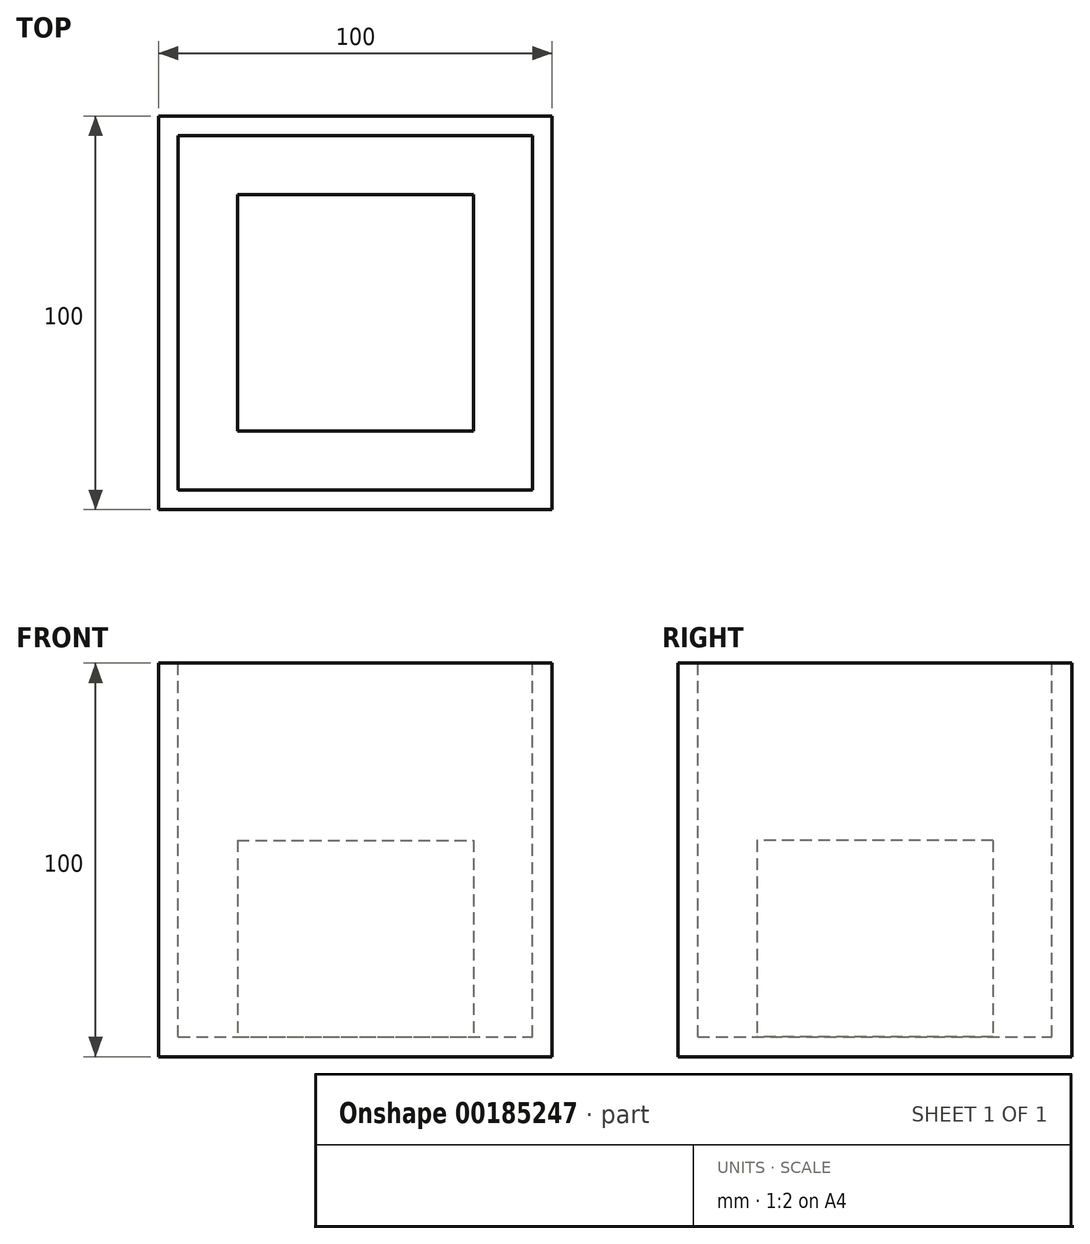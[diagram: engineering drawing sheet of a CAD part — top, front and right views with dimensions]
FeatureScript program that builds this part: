
annotation { "Feature Type Name" : "Feature", "Feature Type Description" : "" }
export const myFeature = defineFeature(function(context is Context, id is Id, definition is map)
    precondition{}
    {
        {
            var Q0;
            Q0=qCreatedBy(makeId("Top.planeOp"),FACE);
            var sketch = newSketch(context, id + "F0", { "sketchPlane" : qUnion([Q0])});
            skLineSegment(sketch, "E0.bottom", {"start": v(0, 0) * mm, "end": v(100, 0) * mm});
            skLineSegment(sketch, "E0.top", {"start": v(0, 100) * mm, "end": v(100, 100) * mm});
            skLineSegment(sketch, "E0.left", {"start": v(0, 0) * mm, "end": v(0, 100) * mm});
            skLineSegment(sketch, "E0.right", {"start": v(100, 0) * mm, "end": v(100, 100) * mm});
            skSolve(sketch);
        }
        {
            var Q0;
            Q0 = qSketchRegion(id + "F0", true);
            extrude(context, id + "F1", {"entities" : qUnion([Q0]), "depth" : 100 * mm});
        }
        {
            var Q0;
            Q0=makeQuery(id+"F1.opExtrude","CAP_FACE",FACE,{"disambiguationData":[OSD([sQuery(id+"F0.wireOp",EDGE,"E0.bottom"),sQuery(id+"F0.wireOp",EDGE,"E0.top"),sQuery(id+"F0.wireOp",EDGE,"E0.left"),sQuery(id+"F0.wireOp",EDGE,"E0.right")])],"isStart":false});
            var sketch = newSketch(context, id + "F2", { "sketchPlane" : qUnion([Q0])});
            skLineSegment(sketch, "E1.bottom", {"start": v(5, 5) * mm, "end": v(95, 5) * mm});
            skLineSegment(sketch, "E1.top", {"start": v(5, 95) * mm, "end": v(95, 95) * mm});
            skLineSegment(sketch, "E1.left", {"start": v(5, 5) * mm, "end": v(5, 95) * mm});
            skLineSegment(sketch, "E1.right", {"start": v(95, 5) * mm, "end": v(95, 95) * mm});
            skSolve(sketch);
        }
        {
            var Q0;
            Q0 = qSketchRegion(id + "F2", true);
            extrude(context, id + "F3", {"entities" : qUnion([Q0]), "operationType" : NewBodyOperationType.REMOVE, "oppositeDirection" : true, "depth" : 95 * mm});
        }
        {
            var Q0;
            Q0=makeQuery(id+"F3.boolean.opBoolean","COPY",FACE,{"derivedFrom":makeQuery(id+"F3.opExtrude","CAP_FACE",FACE,{"disambiguationData":[OSD([sQuery(id+"F2.wireOp",EDGE,"E1.bottom"),sQuery(id+"F2.wireOp",EDGE,"E1.top"),sQuery(id+"F2.wireOp",EDGE,"E1.left"),sQuery(id+"F2.wireOp",EDGE,"E1.right")])],"isStart":false})});
            var sketch = newSketch(context, id + "F4", { "sketchPlane" : qUnion([Q0])});
            skLineSegment(sketch, "E2.bottom", {"start": v(20, 80) * mm, "end": v(80, 80) * mm});
            skLineSegment(sketch, "E2.top", {"start": v(20, 20) * mm, "end": v(80, 20) * mm});
            skLineSegment(sketch, "E2.left", {"start": v(20, 80) * mm, "end": v(20, 20) * mm});
            skLineSegment(sketch, "E2.right", {"start": v(80, 80) * mm, "end": v(80, 20) * mm});
            skSolve(sketch);
        }
        {
            var Q0;
            Q0 = qSketchRegion(id + "F4", true);
            extrude(context, id + "F5", {"entities" : qUnion([Q0]), "operationType" : NewBodyOperationType.ADD, "depth" : 50 * mm});
        }
    });
